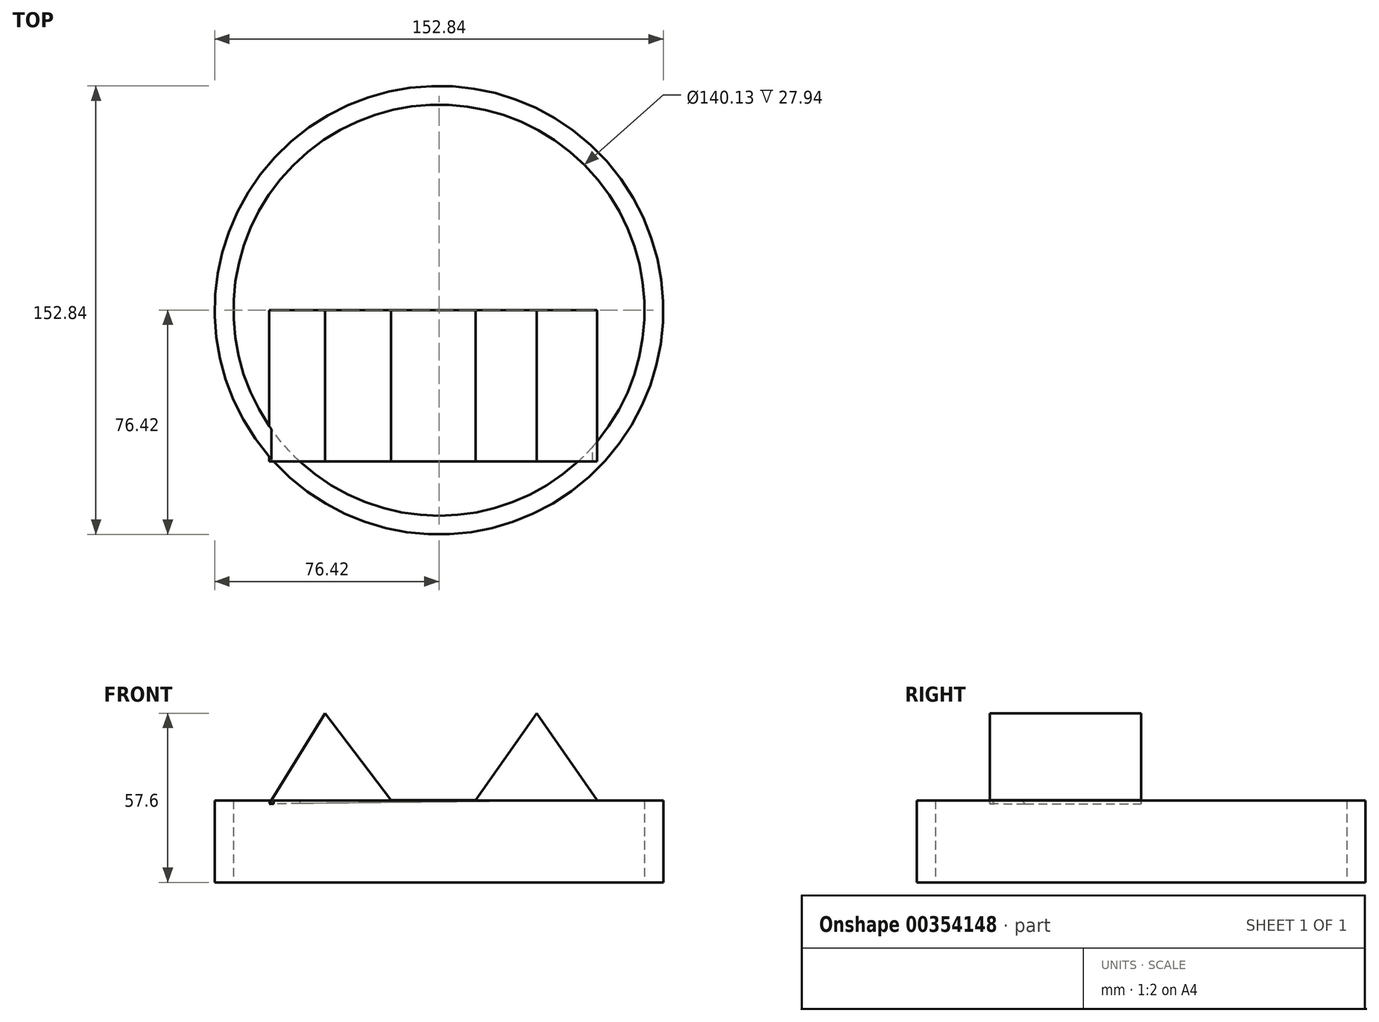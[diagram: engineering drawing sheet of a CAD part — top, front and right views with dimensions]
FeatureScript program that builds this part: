
annotation { "Feature Type Name" : "Feature", "Feature Type Description" : "" }
export const myFeature = defineFeature(function(context is Context, id is Id, definition is map)
    precondition{}
    {
        {
            var Q0;
            Q0=qCreatedBy(makeId("Top.planeOp"),FACE);
            var sketch = newSketch(context, id + "F0", { "sketchPlane" : qUnion([Q0])});
            skCircle(sketch, "E0", {"center": v(0, 0) * mm, "radius": 76.42 * mm});
            skCircle(sketch, "E1", {"center": v(0, 0) * mm, "radius": 70.06 * mm});
            skSolve(sketch);
        }
        {
            var Q0;
            Q0=makeQuery(id+"F0.imprint","IMPRINT",FACE,{"disambiguationData":[TD([[makeQuery(id+"F0.imprint","IMPRINT",EDGE,{"derivedFrom":sQuery(id+"F0.wireOp",EDGE,"E0")}),1.0]])]});
            extrude(context, id + "F1", {"entities" : qUnion([Q0]), "depth" : 27.94 * mm});
        }
        {
            var Q0;
            Q0=qCreatedBy(makeId("Front.planeOp"),FACE);
            var sketch = newSketch(context, id + "F2", { "sketchPlane" : qUnion([Q0])});
            skLineSegment(sketch, "E2", {"start": v(-57.84, 26.75) * mm, "end": v(-38.8, 57.6) * mm});
            skLineSegment(sketch, "E3", {"start": v(-38.8, 57.6) * mm, "end": v(-16.33, 27.96) * mm});
            skLineSegment(sketch, "E4", {"start": v(-16.33, 27.96) * mm, "end": v(12.53, 27.96) * mm});
            skLineSegment(sketch, "E5", {"start": v(12.53, 27.96) * mm, "end": v(33.26, 57.6) * mm});
            skLineSegment(sketch, "E6", {"start": v(33.26, 57.6) * mm, "end": v(53.82, 27.96) * mm});
            skLineSegment(sketch, "E7", {"start": v(53.82, 27.96) * mm, "end": v(-57.84, 26.75) * mm});
            skSolve(sketch);
        }
        {
            var Q0;
            Q0=makeQuery(id+"F2.imprint","IMPRINT",FACE,{"disambiguationData":[TD([[makeQuery(id+"F2.imprint","IMPRINT",EDGE,{"derivedFrom":sQuery(id+"F2.wireOp",EDGE,"E2")}),-1.0]])]});
            extrude(context, id + "F3", {"entities" : qUnion([Q0]), "operationType" : NewBodyOperationType.ADD, "depth" : 51.56 * mm});
        }
    });
